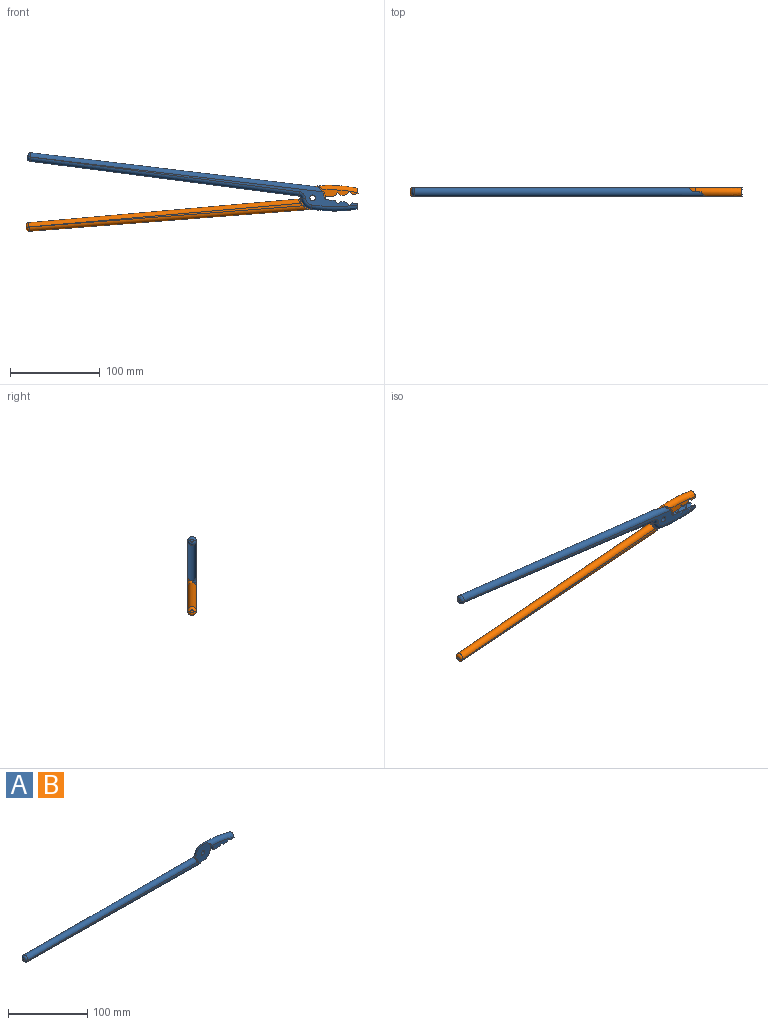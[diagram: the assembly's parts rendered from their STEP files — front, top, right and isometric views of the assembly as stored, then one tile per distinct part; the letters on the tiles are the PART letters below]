
ASSEMBLY  parts=2 mates=1
PART A: 40 faces, bbox 372.9x9.5x27.7 mm
  f0: cylinder r=12.7mm len=12.57mm, axis (0,1,0), area 62.7mm2, adj f16,f18,f30,f38
  f1: plane 305.22x3.31mm, normal (0,-1,0), area 468.9mm2, adj f4,f30,f31,f33,f39
  f2: cylinder r=3.17mm len=6.35mm, axis (0,-1,0), area 95mm2, adj f18,f38
  f3: torus R=157.58mm, axis (0,-1,0), area 699.6mm2, adj f13,f17,f18,f32,f37,f38
  f4: torus R=7.94mm, axis (0,-1,0), area 61.1mm2, adj f1,f18,f31,f32,f38,f39
  f5: plane 9.59x9.53mm, normal (0,0,-1), area 71.2mm2, adj f16,f17,f18,f19,f20,f21,f24,f29
  f6: plane 6.35x1.59mm, normal (0,0,-1), area 10.1mm2, adj f9,f18,f27,f28
  f7: plane 6.35x1.59mm, normal (0,0,-1), area 10.1mm2, adj f11,f17,f22,f25
  f8: plane 6.35x1.59mm, normal (0,0,-1), area 10.1mm2, adj f10,f13,f18,f26
  f9: plane 12.7x3.18mm, normal (0,-0.71,-0.71), area 42.8mm2, adj f6,f11,f27,f28
  f10: plane 9.53x3.18mm, normal (0,-0.71,-0.71), area 35.6mm2, adj f8,f12,f13,f26
  f11: plane 12.7x3.18mm, normal (0,0.71,-0.71), area 42.8mm2, adj f7,f9,f22,f25
  f12: plane 9.53x3.18mm, normal (0,0.71,-0.71), area 35.6mm2, adj f10,f13,f14,f23
  f13: plane 9.53x6.35mm, normal (1,0,0), area 40.3mm2, adj f3,f8,f10,f12,f14,f17,f18
  f14: plane 6.35x1.59mm, normal (0,0,-1), area 10.1mm2, adj f12,f13,f17,f23
  f15: plane 3.21x3.18mm, normal (-1,0,0), area 8mm2, adj f33,f34,f35,f36
  f16: cylinder r=3.17mm len=9.53mm, axis (0,1,0), area 26.9mm2, adj f0,f5,f17,f18,f37,f38
  f17: plane 38.63x8.15mm, normal (0,-1,0), area 178.2mm2, adj f3,f5,f7,f13,f14,f16,f22,f23
  f18: plane 367.72x16.06mm, normal (0,1,0), area 957.4mm2, adj f0,f2,f3,f4,f5,f6,f8,f13
  f19: plane 6.35x3.18mm, normal (0,-0.71,-0.71), area 21.4mm2, adj f5,f20,f21,f29
  f20: plane 6.35x3.18mm, normal (0,0.71,-0.71), area 21.4mm2, adj f5,f19,f21,f24
  f21: plane 6.35x3.18mm, normal (1,0,0), area 10.1mm2, adj f5,f19,f20
  f22: plane 4.76x3.18mm, normal (0.71,0,-0.71), area 14.3mm2, adj f7,f11,f17,f23
  f23: plane 4.76x3.18mm, normal (-0.71,0,-0.71), area 14.3mm2, adj f12,f14,f17,f22
  f24: plane 4.76x3.18mm, normal (0.71,0,-0.71), area 14.3mm2, adj f5,f17,f20,f25
  f25: plane 4.76x3.18mm, normal (-0.71,0,-0.71), area 14.3mm2, adj f7,f11,f17,f24
  f26: plane 4.76x3.18mm, normal (-0.71,0,-0.71), area 14.3mm2, adj f8,f10,f18,f27
  f27: plane 4.76x3.18mm, normal (0.71,0,-0.71), area 14.3mm2, adj f6,f9,f18,f26
  f28: plane 4.76x3.18mm, normal (-0.71,0,-0.71), area 14.3mm2, adj f6,f9,f18,f29
  f29: plane 4.76x3.18mm, normal (0.71,0,-0.71), area 14.3mm2, adj f5,f18,f19,f28
  f30: cylinder r=4.76mm len=327.06mm, axis (-1,0,0.01), area 4719.4mm2, adj f0,f1,f18,f35,f38,f39
  f31: cylinder r=4.76mm len=301.63mm, axis (1,0,0), area 4512.9mm2, adj f1,f4,f18,f34
  f32: torus R=7.94mm, axis (0,-1,0), area 112.7mm2, adj f3,f4,f18,f38
  f33: cylinder r=3.17mm len=3.18mm, axis (0,0,-1), area 0.2mm2, adj f1,f15,f34,f35
  f34: torus R=1.59mm, axis (1,0,0), area 56.5mm2, adj f15,f31,f33,f36
  f35: bspline ~9.53x5.59mm, area 56.2mm2, adj f15,f30,f33,f36
  f36: cylinder r=3.17mm len=3.18mm, axis (0,0,-1), area 0.2mm2, adj f15,f18,f34,f35
  f37: cylinder r=14.29mm len=13.05mm, axis (0,-1,0), area 67.6mm2, adj f3,f16,f17,f38
  f38: plane 28.58x25.49mm, normal (0,-1,0), area 531.4mm2, adj f0,f2,f3,f4,f16,f30,f32,f37
  f39: cylinder r=14.29mm len=12.9mm, axis (0,-1,0), area 61.3mm2, adj f1,f4,f30,f38
PART B: same geometry as A
PLACE A rot(axis=(1,0,-0.06),180deg) t=(-17.25,-88.73,23.25)mm
PLACE B rot(axis=(0,-1,0),5deg) t=(-17.25,-79.2,23.25)mm
MATE revolute B.f2 <-> A.f2  axis (0,-1,0) through (-17.25,-83.96,23.25)mm
